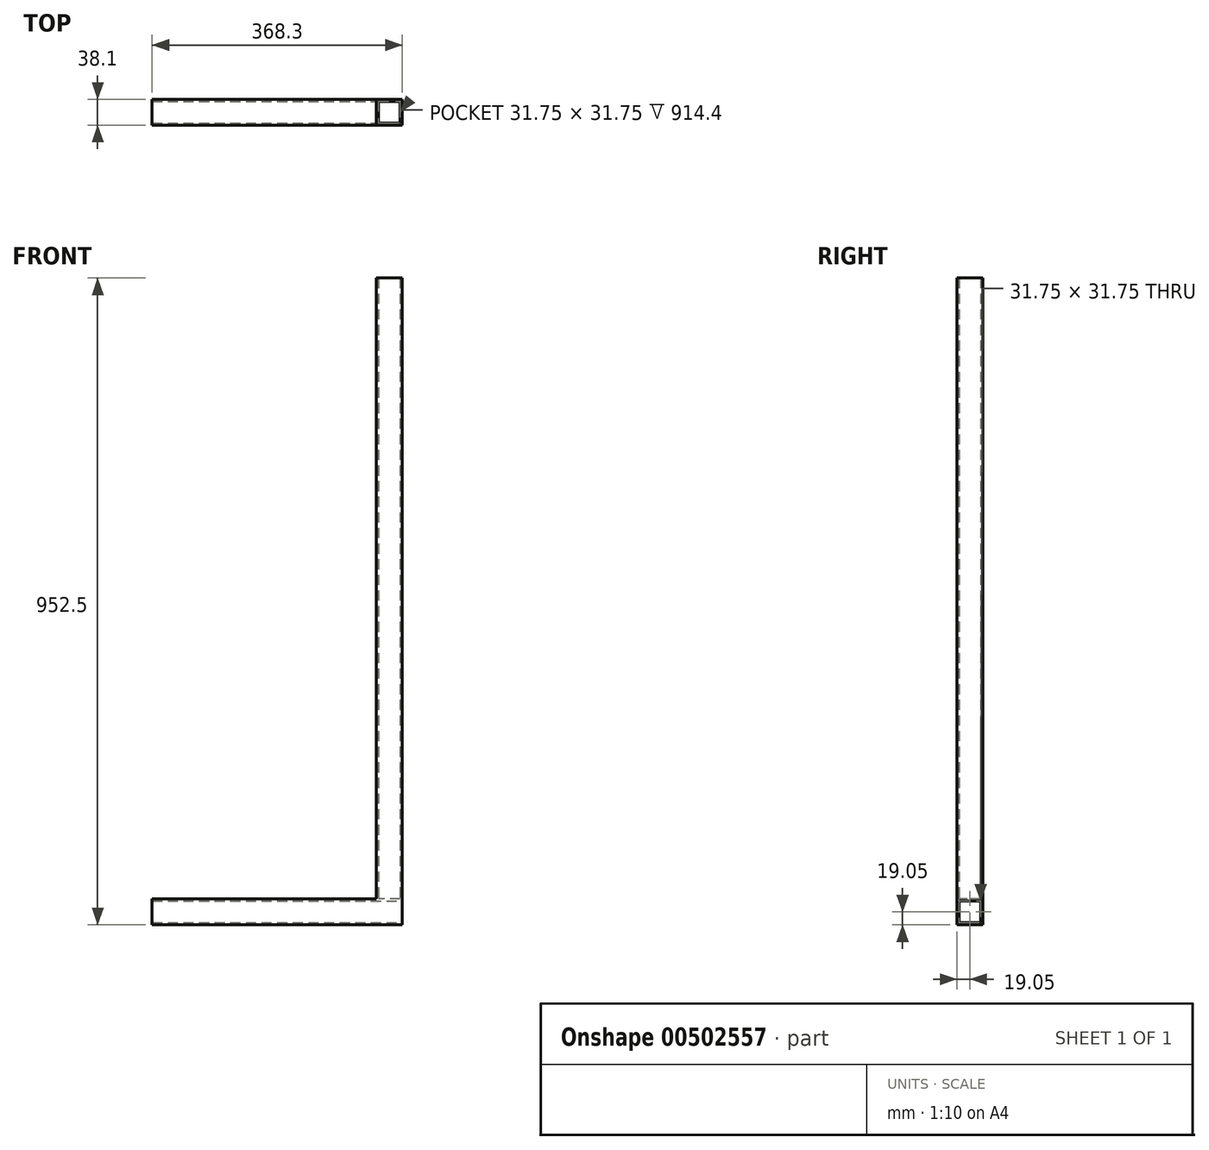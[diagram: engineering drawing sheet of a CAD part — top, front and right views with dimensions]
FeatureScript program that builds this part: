
annotation { "Feature Type Name" : "Feature", "Feature Type Description" : "" }
export const myFeature = defineFeature(function(context is Context, id is Id, definition is map)
    precondition{}
    {
        {
            var Q0;
            Q0=qCreatedBy(makeId("Right.planeOp"),FACE);
            var sketch = newSketch(context, id + "F0", { "sketchPlane" : qUnion([Q0])});
            skLineSegment(sketch, "E0.bottom", {"start": v(19.05, -19.05) * mm, "end": v(-19.05, -19.05) * mm});
            skLineSegment(sketch, "E0.top", {"start": v(19.05, 19.05) * mm, "end": v(-19.05, 19.05) * mm});
            skLineSegment(sketch, "E0.left", {"start": v(19.05, -19.05) * mm, "end": v(19.05, 19.05) * mm});
            skLineSegment(sketch, "E0.right", {"start": v(-19.05, -19.05) * mm, "end": v(-19.05, 19.05) * mm});
            skPoint(sketch, "E0.middle", {"position": v(0, 0) * mm});
            skLineSegment(sketch, "E1.bottom", {"start": v(15.88, 15.88) * mm, "end": v(-15.88, 15.87) * mm});
            skLineSegment(sketch, "E1.top", {"start": v(15.88, -15.87) * mm, "end": v(-15.88, -15.88) * mm});
            skLineSegment(sketch, "E1.left", {"start": v(15.88, 15.88) * mm, "end": v(15.88, -15.87) * mm});
            skLineSegment(sketch, "E1.right", {"start": v(-15.88, 15.87) * mm, "end": v(-15.88, -15.88) * mm});
            skSolve(sketch);
        }
        {
            var Q0;
            Q0=makeQuery(id+"F0.imprint","IMPRINT",FACE,{"disambiguationData":[TD([[makeQuery(id+"F0.imprint","IMPRINT",EDGE,{"derivedFrom":sQuery(id+"F0.wireOp",EDGE,"E0.bottom")}),-1.0]])]});
            extrude(context, id + "F1", {"entities" : qUnion([Q0]), "oppositeDirection" : true, "depth" : 368.3 * mm, "offsetDistance" : 25.4 * mm});
        }
        {
            var Q0;
            Q0=makeQuery(id+"F1.opExtrude","SWEPT_FACE",FACE,{"disambiguationData":[OSD([sQuery(id+"F0.wireOp",EDGE,"E0.top")])]});
            var sketch = newSketch(context, id + "F2", { "sketchPlane" : qUnion([Q0])});
            skLineSegment(sketch, "E2.bottom", {"start": v(0, 19.05) * mm, "end": v(-38.1, 19.05) * mm});
            skLineSegment(sketch, "E2.top", {"start": v(0, -19.05) * mm, "end": v(-38.1, -19.05) * mm});
            skLineSegment(sketch, "E2.left", {"start": v(0, 19.05) * mm, "end": v(0, -19.05) * mm});
            skLineSegment(sketch, "E2.right", {"start": v(-38.1, 19.05) * mm, "end": v(-38.1, -19.05) * mm});
            skLineSegment(sketch, "E3.bottom", {"start": v(-3.17, 15.88) * mm, "end": v(-34.93, 15.87) * mm});
            skLineSegment(sketch, "E3.top", {"start": v(-3.17, -15.87) * mm, "end": v(-34.93, -15.88) * mm});
            skLineSegment(sketch, "E3.left", {"start": v(-3.18, 15.88) * mm, "end": v(-3.17, -15.88) * mm});
            skLineSegment(sketch, "E3.right", {"start": v(-34.93, 15.88) * mm, "end": v(-34.92, -15.88) * mm});
            skSolve(sketch);
        }
        {
            var Q0;
            Q0=makeQuery(id+"F2.imprint","IMPRINT",FACE,{"disambiguationData":[TD([[makeQuery(id+"F2.imprint","IMPRINT",EDGE,{"derivedFrom":sQuery(id+"F2.wireOp",EDGE,"E2.bottom")}),-1.0]])]});
            extrude(context, id + "F3", {"entities" : qUnion([Q0]), "operationType" : NewBodyOperationType.ADD, "depth" : 914.4 * mm, "offsetDistance" : 25.4 * mm});
        }
    });
